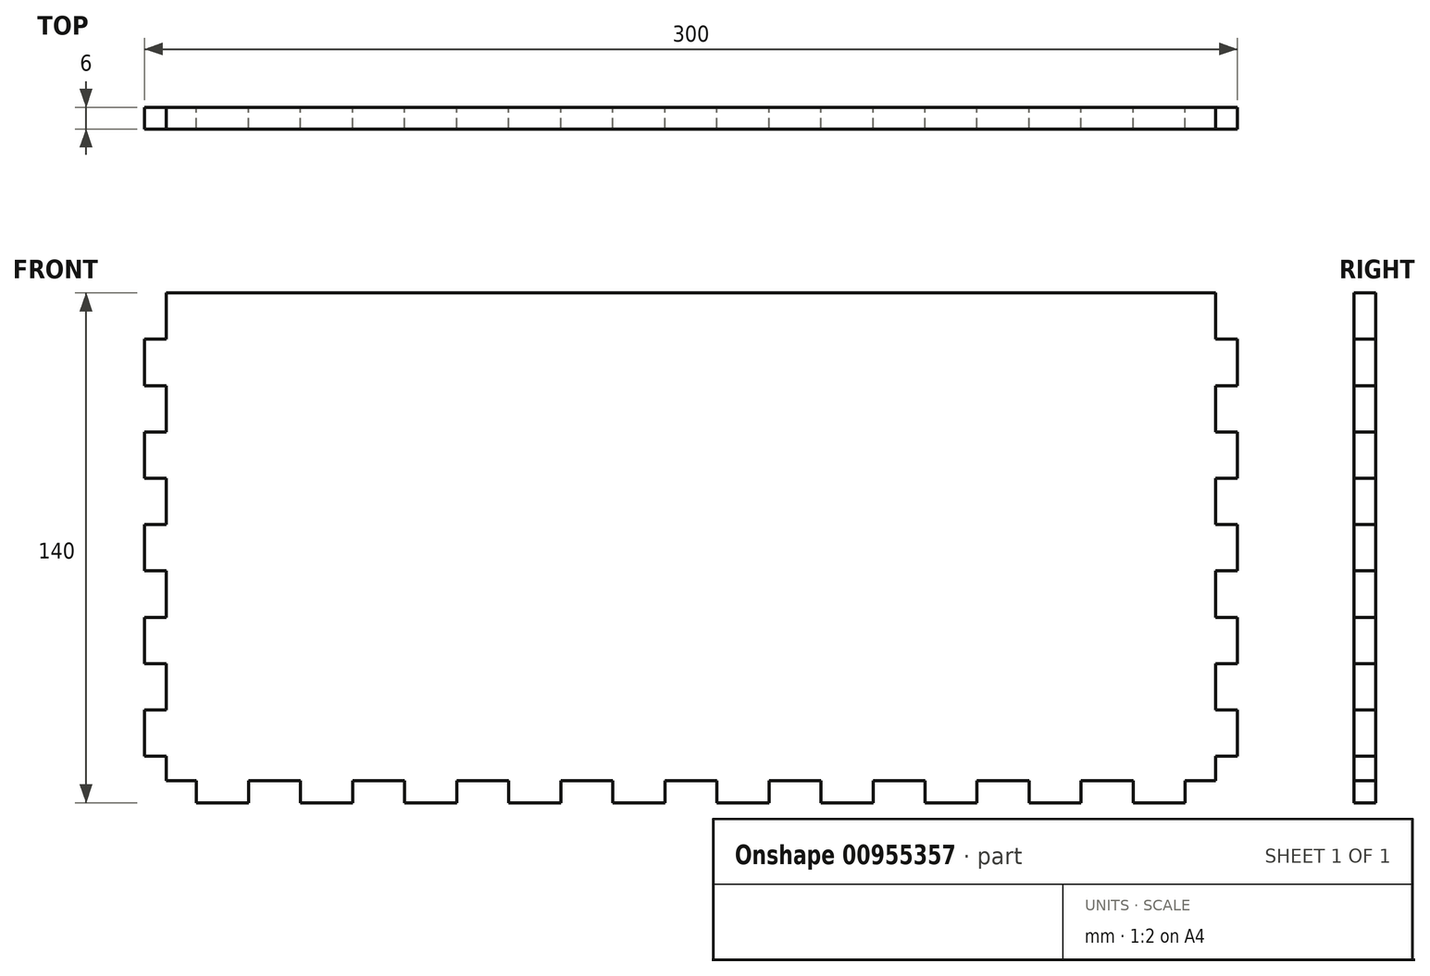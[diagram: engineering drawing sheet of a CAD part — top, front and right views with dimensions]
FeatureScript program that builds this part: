
annotation { "Feature Type Name" : "Feature", "Feature Type Description" : "" }
export const myFeature = defineFeature(function(context is Context, id is Id, definition is map)
    precondition{}
    {
        {
            var Q0;
            Q0=qCreatedBy(makeId("Front.planeOp"),FACE);
            var sketch = newSketch(context, id + "F0", { "sketchPlane" : qUnion([Q0])});
            skLineSegment(sketch, "E0.top", {"start": v(144, 70) * mm, "end": v(-144, 70) * mm});
            skPoint(sketch, "E0.middle", {"position": v(0, 0) * mm});
            skLineSegment(sketch, "E1", {"start": v(-144, -64) * mm, "end": v(-135.71, -64) * mm});
            skLineSegment(sketch, "E2", {"start": v(-135.71, -64) * mm, "end": v(-135.71, -70) * mm});
            skLineSegment(sketch, "E3", {"start": v(-135.71, -70) * mm, "end": v(-121.43, -70) * mm});
            skLineSegment(sketch, "E4", {"start": v(-121.43, -70) * mm, "end": v(-121.43, -64) * mm});
            skLineSegment(sketch, "E5", {"start": v(-121.43, -64) * mm, "end": v(-107.14, -64) * mm});
            skLineSegment(sketch, "E6.1.0.0", {"start": v(-92.86, -64) * mm, "end": v(-78.57, -64) * mm});
            skLineSegment(sketch, "E6.1.0.1", {"start": v(-107.14, -64) * mm, "end": v(-107.14, -70) * mm});
            skLineSegment(sketch, "E6.1.0.2", {"start": v(-92.86, -70) * mm, "end": v(-92.86, -64) * mm});
            skLineSegment(sketch, "E6.1.0.3", {"start": v(-107.14, -70) * mm, "end": v(-92.86, -70) * mm});
            skLineSegment(sketch, "E6.2.0.0", {"start": v(-64.29, -64) * mm, "end": v(-50, -64) * mm});
            skLineSegment(sketch, "E6.2.0.1", {"start": v(-78.57, -64) * mm, "end": v(-78.57, -70) * mm});
            skLineSegment(sketch, "E6.2.0.2", {"start": v(-64.29, -70) * mm, "end": v(-64.29, -64) * mm});
            skLineSegment(sketch, "E6.2.0.3", {"start": v(-78.57, -70) * mm, "end": v(-64.29, -70) * mm});
            skLineSegment(sketch, "E6.2.0.4", {"start": v(-92.86, -64) * mm, "end": v(-78.57, -64) * mm});
            skLineSegment(sketch, "E6.3.0.0", {"start": v(-35.71, -64) * mm, "end": v(-21.43, -64) * mm});
            skLineSegment(sketch, "E6.3.0.1", {"start": v(-50, -64) * mm, "end": v(-50, -70) * mm});
            skLineSegment(sketch, "E6.3.0.2", {"start": v(-35.71, -70) * mm, "end": v(-35.71, -64) * mm});
            skLineSegment(sketch, "E6.3.0.3", {"start": v(-50, -70) * mm, "end": v(-35.71, -70) * mm});
            skLineSegment(sketch, "E6.3.0.4", {"start": v(-64.29, -64) * mm, "end": v(-50, -64) * mm});
            skLineSegment(sketch, "E6.4.0.0", {"start": v(-7.14, -64) * mm, "end": v(7.14, -64) * mm});
            skLineSegment(sketch, "E6.4.0.1", {"start": v(-21.43, -64) * mm, "end": v(-21.43, -70) * mm});
            skLineSegment(sketch, "E6.4.0.2", {"start": v(-7.14, -70) * mm, "end": v(-7.14, -64) * mm});
            skLineSegment(sketch, "E6.4.0.3", {"start": v(-21.43, -70) * mm, "end": v(-7.14, -70) * mm});
            skLineSegment(sketch, "E6.4.0.4", {"start": v(-35.71, -64) * mm, "end": v(-21.43, -64) * mm});
            skLineSegment(sketch, "E6.5.0.0", {"start": v(21.43, -64) * mm, "end": v(35.71, -64) * mm});
            skLineSegment(sketch, "E6.5.0.1", {"start": v(7.14, -64) * mm, "end": v(7.14, -70) * mm});
            skLineSegment(sketch, "E6.5.0.2", {"start": v(21.43, -70) * mm, "end": v(21.43, -64) * mm});
            skLineSegment(sketch, "E6.5.0.3", {"start": v(7.14, -70) * mm, "end": v(21.43, -70) * mm});
            skLineSegment(sketch, "E6.5.0.4", {"start": v(-7.14, -64) * mm, "end": v(7.14, -64) * mm});
            skLineSegment(sketch, "E6.6.0.0", {"start": v(50, -64) * mm, "end": v(64.29, -64) * mm});
            skLineSegment(sketch, "E6.6.0.1", {"start": v(35.71, -64) * mm, "end": v(35.71, -70) * mm});
            skLineSegment(sketch, "E6.6.0.2", {"start": v(50, -70) * mm, "end": v(50, -64) * mm});
            skLineSegment(sketch, "E6.6.0.3", {"start": v(35.71, -70) * mm, "end": v(50, -70) * mm});
            skLineSegment(sketch, "E6.6.0.4", {"start": v(21.43, -64) * mm, "end": v(35.71, -64) * mm});
            skLineSegment(sketch, "E6.7.0.0", {"start": v(78.57, -64) * mm, "end": v(92.86, -64) * mm});
            skLineSegment(sketch, "E6.7.0.1", {"start": v(64.29, -64) * mm, "end": v(64.29, -70) * mm});
            skLineSegment(sketch, "E6.7.0.2", {"start": v(78.57, -70) * mm, "end": v(78.57, -64) * mm});
            skLineSegment(sketch, "E6.7.0.3", {"start": v(64.29, -70) * mm, "end": v(78.57, -70) * mm});
            skLineSegment(sketch, "E6.7.0.4", {"start": v(50, -64) * mm, "end": v(64.29, -64) * mm});
            skLineSegment(sketch, "E6.8.0.0", {"start": v(107.14, -64) * mm, "end": v(121.43, -64) * mm});
            skLineSegment(sketch, "E6.8.0.1", {"start": v(92.86, -64) * mm, "end": v(92.86, -70) * mm});
            skLineSegment(sketch, "E6.8.0.2", {"start": v(107.14, -70) * mm, "end": v(107.14, -64) * mm});
            skLineSegment(sketch, "E6.8.0.3", {"start": v(92.86, -70) * mm, "end": v(107.14, -70) * mm});
            skLineSegment(sketch, "E6.8.0.4", {"start": v(78.57, -64) * mm, "end": v(92.86, -64) * mm});
            skLineSegment(sketch, "E6.9.0.0", {"start": v(135.71, -64) * mm, "end": v(144, -64) * mm});
            skLineSegment(sketch, "E6.9.0.1", {"start": v(121.43, -64) * mm, "end": v(121.43, -70) * mm});
            skLineSegment(sketch, "E6.9.0.2", {"start": v(135.71, -70) * mm, "end": v(135.71, -64) * mm});
            skLineSegment(sketch, "E6.9.0.3", {"start": v(121.43, -70) * mm, "end": v(135.71, -70) * mm});
            skLineSegment(sketch, "E6.9.0.4", {"start": v(107.14, -64) * mm, "end": v(121.43, -64) * mm});
            skLineSegment(sketch, "E6.direction1", {"start": v(-144, -64) * mm, "end": v(-121.43, -64) * mm, "construction": true});
            skPoint(sketch, "E7.orphan", {"position": v(-150, -70) * mm});
            skPoint(sketch, "E8.orphan", {"position": v(150, -70) * mm});
            skLineSegment(sketch, "E9", {"start": v(-144, -64) * mm, "end": v(-144, -57.27) * mm});
            skLineSegment(sketch, "E10", {"start": v(-144, -57.27) * mm, "end": v(-150, -57.27) * mm});
            skLineSegment(sketch, "E11", {"start": v(-150, -57.27) * mm, "end": v(-150, -44.55) * mm});
            skLineSegment(sketch, "E12", {"start": v(-150, -44.55) * mm, "end": v(-144, -44.55) * mm});
            skLineSegment(sketch, "E13", {"start": v(-144, -44.55) * mm, "end": v(-144, -31.82) * mm});
            skPoint(sketch, "E14.orphan", {"position": v(-150, -64) * mm});
            skLineSegment(sketch, "E15.1.0.0", {"start": v(-144, -38.55) * mm, "end": v(-144, -31.82) * mm});
            skLineSegment(sketch, "E15.1.0.1", {"start": v(-144, -31.82) * mm, "end": v(-150, -31.82) * mm});
            skLineSegment(sketch, "E15.1.0.2", {"start": v(-150, -19.1) * mm, "end": v(-144, -19.1) * mm});
            skLineSegment(sketch, "E15.1.0.3", {"start": v(-150, -31.82) * mm, "end": v(-150, -19.1) * mm});
            skPoint(sketch, "E15.1.0.4", {"position": v(-150, -44.55) * mm});
            skLineSegment(sketch, "E15.1.0.5", {"start": v(-144, -19.1) * mm, "end": v(-144, -6.36) * mm});
            skPoint(sketch, "E15.1.0.6", {"position": v(-150, -38.55) * mm});
            skLineSegment(sketch, "E15.2.0.0", {"start": v(-144, -13.1) * mm, "end": v(-144, -6.36) * mm});
            skLineSegment(sketch, "E15.2.0.1", {"start": v(-144, -6.36) * mm, "end": v(-150, -6.36) * mm});
            skLineSegment(sketch, "E15.2.0.2", {"start": v(-150, 6.36) * mm, "end": v(-144, 6.36) * mm});
            skLineSegment(sketch, "E15.2.0.3", {"start": v(-150, -6.36) * mm, "end": v(-150, 6.36) * mm});
            skPoint(sketch, "E15.2.0.4", {"position": v(-150, -19.1) * mm});
            skLineSegment(sketch, "E15.2.0.5", {"start": v(-144, 6.36) * mm, "end": v(-144, 19.1) * mm});
            skPoint(sketch, "E15.2.0.6", {"position": v(-150, -13.1) * mm});
            skLineSegment(sketch, "E15.3.0.0", {"start": v(-144, 12.36) * mm, "end": v(-144, 19.1) * mm});
            skLineSegment(sketch, "E15.3.0.1", {"start": v(-144, 19.1) * mm, "end": v(-150, 19.1) * mm});
            skLineSegment(sketch, "E15.3.0.2", {"start": v(-150, 31.82) * mm, "end": v(-144, 31.82) * mm});
            skLineSegment(sketch, "E15.3.0.3", {"start": v(-150, 19.1) * mm, "end": v(-150, 31.82) * mm});
            skPoint(sketch, "E15.3.0.4", {"position": v(-150, 6.36) * mm});
            skLineSegment(sketch, "E15.3.0.5", {"start": v(-144, 31.82) * mm, "end": v(-144, 44.55) * mm});
            skPoint(sketch, "E15.3.0.6", {"position": v(-150, 12.36) * mm});
            skLineSegment(sketch, "E15.4.0.0", {"start": v(-144, 37.82) * mm, "end": v(-144, 44.55) * mm});
            skLineSegment(sketch, "E15.4.0.1", {"start": v(-144, 44.55) * mm, "end": v(-150, 44.55) * mm});
            skLineSegment(sketch, "E15.4.0.2", {"start": v(-150, 57.27) * mm, "end": v(-144, 57.27) * mm});
            skLineSegment(sketch, "E15.4.0.3", {"start": v(-150, 44.55) * mm, "end": v(-150, 57.27) * mm});
            skPoint(sketch, "E15.4.0.4", {"position": v(-150, 31.82) * mm});
            skLineSegment(sketch, "E15.4.0.5", {"start": v(-144, 57.27) * mm, "end": v(-144, 70) * mm});
            skPoint(sketch, "E15.4.0.6", {"position": v(-150, 37.82) * mm});
            skLineSegment(sketch, "E15.direction1", {"start": v(-144, -64) * mm, "end": v(-144, -38.55) * mm, "construction": true});
            skPoint(sketch, "E16.orphan", {"position": v(-150, 70) * mm});
            skLineSegment(sketch, "E17.MirrorCS", {"start": v(144, -64) * mm, "end": v(144, -57.27) * mm});
            skLineSegment(sketch, "E18.MirrorCS", {"start": v(144, 37.82) * mm, "end": v(144, 44.55) * mm});
            skLineSegment(sketch, "E19.MirrorCS", {"start": v(144, -38.55) * mm, "end": v(144, -31.82) * mm});
            skLineSegment(sketch, "E20.MirrorCS", {"start": v(150, -57.27) * mm, "end": v(150, -44.55) * mm});
            skLineSegment(sketch, "E21.MirrorCS", {"start": v(144, 19.1) * mm, "end": v(150, 19.1) * mm});
            skLineSegment(sketch, "E22.MirrorCS", {"start": v(144, -64) * mm, "end": v(135.71, -64) * mm});
            skLineSegment(sketch, "E23.MirrorCS", {"start": v(144, -44.55) * mm, "end": v(144, -31.82) * mm});
            skLineSegment(sketch, "E24.MirrorCS", {"start": v(150, 6.36) * mm, "end": v(144, 6.36) * mm});
            skLineSegment(sketch, "E25.MirrorCS", {"start": v(144, -6.36) * mm, "end": v(150, -6.36) * mm});
            skLineSegment(sketch, "E26.MirrorCS", {"start": v(144, 31.82) * mm, "end": v(144, 44.55) * mm});
            skLineSegment(sketch, "E27.MirrorCS", {"start": v(144, 12.36) * mm, "end": v(144, 19.1) * mm});
            skLineSegment(sketch, "E28.MirrorCS", {"start": v(144, 6.36) * mm, "end": v(144, 19.1) * mm});
            skLineSegment(sketch, "E29.MirrorCS", {"start": v(144, -57.27) * mm, "end": v(150, -57.27) * mm});
            skLineSegment(sketch, "E30.MirrorCS", {"start": v(144, 44.55) * mm, "end": v(150, 44.55) * mm});
            skLineSegment(sketch, "E31.MirrorCS", {"start": v(150, -44.55) * mm, "end": v(144, -44.55) * mm});
            skLineSegment(sketch, "E32.MirrorCS", {"start": v(144, -31.82) * mm, "end": v(150, -31.82) * mm});
            skLineSegment(sketch, "E33.MirrorCS", {"start": v(150, -19.1) * mm, "end": v(144, -19.1) * mm});
            skLineSegment(sketch, "E34.MirrorCS", {"start": v(150, 44.55) * mm, "end": v(150, 57.27) * mm});
            skLineSegment(sketch, "E35.MirrorCS", {"start": v(144, -19.1) * mm, "end": v(144, -6.36) * mm});
            skLineSegment(sketch, "E36.MirrorCS", {"start": v(150, 57.27) * mm, "end": v(144, 57.27) * mm});
            skLineSegment(sketch, "E37.MirrorCS", {"start": v(150, -31.82) * mm, "end": v(150, -19.1) * mm});
            skLineSegment(sketch, "E38.MirrorCS", {"start": v(150, -6.36) * mm, "end": v(150, 6.36) * mm});
            skLineSegment(sketch, "E39.MirrorCS", {"start": v(135.71, -64) * mm, "end": v(135.71, -70) * mm});
            skLineSegment(sketch, "E40.MirrorCS", {"start": v(150, 19.1) * mm, "end": v(150, 31.82) * mm});
            skLineSegment(sketch, "E41.MirrorCS", {"start": v(144, 57.27) * mm, "end": v(144, 70) * mm});
            skLineSegment(sketch, "E42.MirrorCS", {"start": v(150, 31.82) * mm, "end": v(144, 31.82) * mm});
            skLineSegment(sketch, "E43.MirrorCS", {"start": v(144, -13.1) * mm, "end": v(144, -6.36) * mm});
            skLineSegment(sketch, "E44.MirrorCS", {"start": v(144, -64) * mm, "end": v(144, -38.55) * mm, "construction": true});
            skPoint(sketch, "E45.MirrorP", {"position": v(150, -44.55) * mm});
            skPoint(sketch, "E46.MirrorP", {"position": v(150, -38.55) * mm});
            skPoint(sketch, "E47.MirrorP", {"position": v(150, 70) * mm});
            skPoint(sketch, "E48.MirrorP", {"position": v(150, -19.1) * mm});
            skPoint(sketch, "E49.MirrorP", {"position": v(150, 12.36) * mm});
            skPoint(sketch, "E50.MirrorP", {"position": v(150, 31.82) * mm});
            skPoint(sketch, "E51.MirrorP", {"position": v(150, 6.36) * mm});
            skPoint(sketch, "E52.MirrorP", {"position": v(150, 37.82) * mm});
            skPoint(sketch, "E53.MirrorP", {"position": v(150, -64) * mm});
            skPoint(sketch, "E54.MirrorP", {"position": v(150, -13.1) * mm});
            skSolve(sketch);
        }
        {
            var Q0;
            Q0=makeQuery(id+"F0.imprint","IMPRINT",FACE,{"disambiguationData":[TD([[makeQuery(id+"F0.imprint","IMPRINT",EDGE,{"derivedFrom":sQuery(id+"F0.wireOp",EDGE,"E0.top")}),1.0]])]});
            extrude(context, id + "F1", {"entities" : qUnion([Q0]), "depth" : 6 * mm, "offsetDistance" : 25 * mm});
        }
    });
